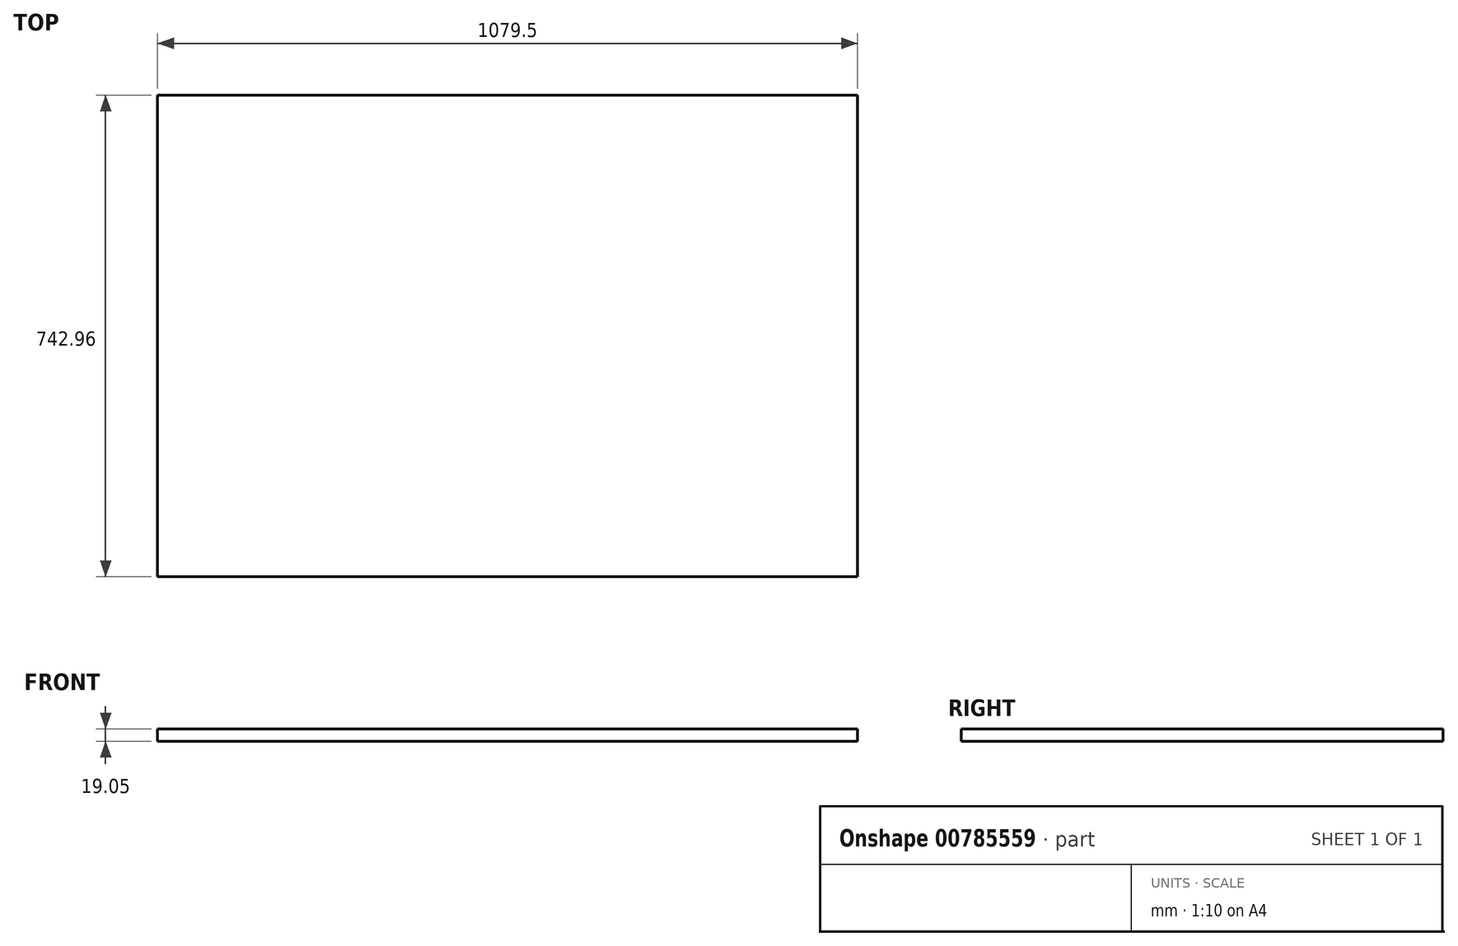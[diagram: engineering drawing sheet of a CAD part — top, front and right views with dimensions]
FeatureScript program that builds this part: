
annotation { "Feature Type Name" : "Feature", "Feature Type Description" : "" }
export const myFeature = defineFeature(function(context is Context, id is Id, definition is map)
    precondition{}
    {
        {
            var Q0;
            Q0=qCreatedBy(makeId("Top.planeOp"),FACE);
            var sketch = newSketch(context, id + "F0", { "sketchPlane" : qUnion([Q0])});
            skLineSegment(sketch, "E0.bottom", {"start": v(539.75, 371.48) * mm, "end": v(-539.75, 371.48) * mm});
            skLineSegment(sketch, "E0.top", {"start": v(539.75, -371.48) * mm, "end": v(-539.75, -371.48) * mm});
            skLineSegment(sketch, "E0.left", {"start": v(539.75, 371.48) * mm, "end": v(539.75, -371.48) * mm});
            skLineSegment(sketch, "E0.right", {"start": v(-539.75, 371.48) * mm, "end": v(-539.75, -371.48) * mm});
            skPoint(sketch, "E0.middle", {"position": v(0, 0) * mm});
            skSolve(sketch);
        }
        {
            var Q0;
            Q0 = qSketchRegion(id + "F0", true);
            extrude(context, id + "F1", {"entities" : qUnion([Q0]), "depth" : 19.05 * mm, "offsetDistance" : 25.4 * mm});
        }
    });
